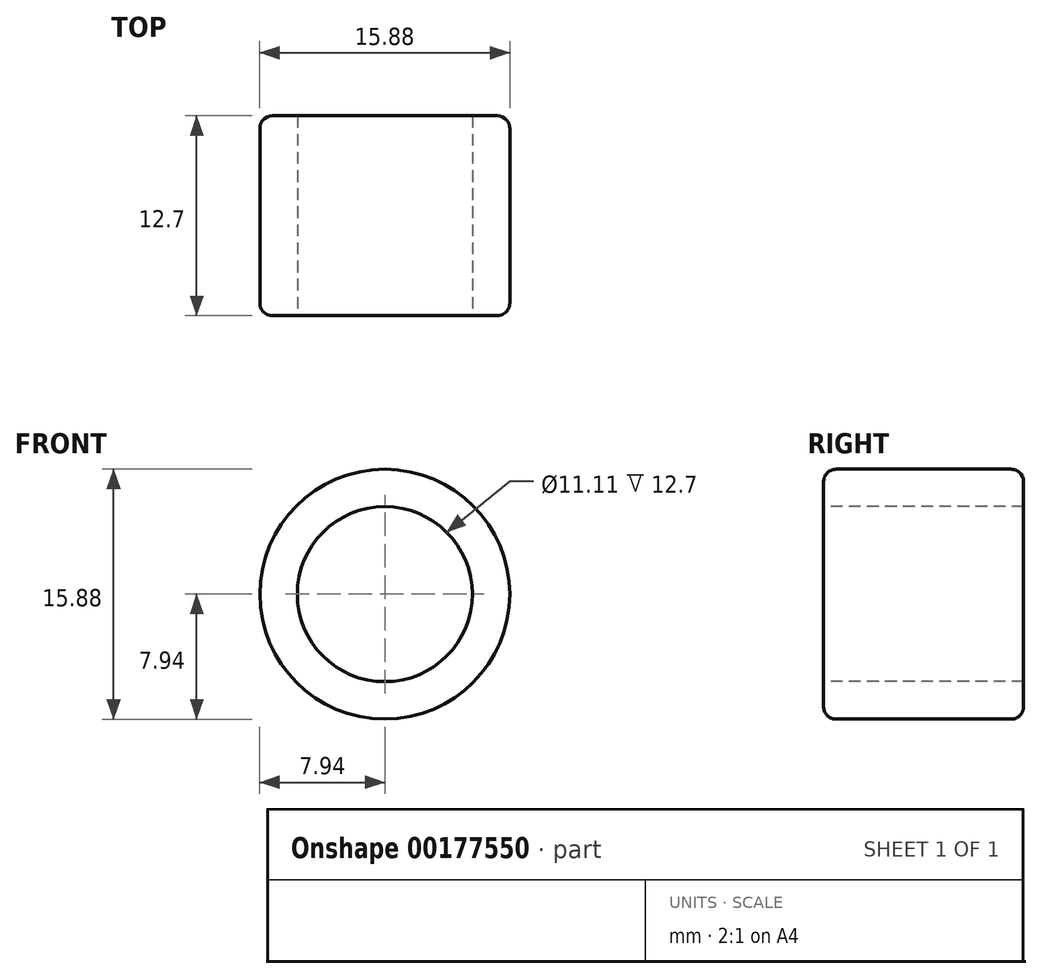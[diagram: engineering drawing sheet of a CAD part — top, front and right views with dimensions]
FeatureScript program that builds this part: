
annotation { "Feature Type Name" : "Feature", "Feature Type Description" : "" }
export const myFeature = defineFeature(function(context is Context, id is Id, definition is map)
    precondition{}
    {
        {
            var Q0;
            Q0=qCreatedBy(makeId("Front.planeOp"),FACE);
            var sketch = newSketch(context, id + "F0", { "sketchPlane" : qUnion([Q0])});
            skCircle(sketch, "E0", {"center": v(0, 0) * mm, "radius": 5.56 * mm});
            skCircle(sketch, "E1", {"center": v(0, 0) * mm, "radius": 7.94 * mm});
            skSolve(sketch);
        }
        {
            var Q0;
            Q0 = qSketchRegion(id + "F0", true);
            extrude(context, id + "F1", {"entities" : qUnion([Q0]), "oppositeDirection" : true, "depth" : 12.7 * mm});
        }
        {
            var Q0;
            Q0=makeQuery(id+"F1.opExtrude","CAP_EDGE",EDGE,{"disambiguationData":[OSD([sQuery(id+"F0.wireOp",EDGE,"E1")])],"isStart":true});
            var Q1;
            Q1=makeQuery(id+"F1.opExtrude","CAP_EDGE",EDGE,{"disambiguationData":[OSD([sQuery(id+"F0.wireOp",EDGE,"E1")])],"isStart":false});
            fillet(context, id + "F2", {"entities" : qUnion([Q0, Q1]), "radius" : 0.8 * mm, "tangentPropagation" : true, "allowEdgeOverflow" : false});
        }
    });
